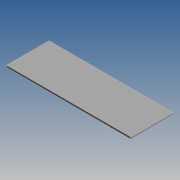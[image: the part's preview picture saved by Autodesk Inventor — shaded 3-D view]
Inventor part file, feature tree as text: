
AUTODESK INVENTOR PART (.ipt)
format: ipt  version: 2015 SP1 (Build 190203100, 203)  size: 176,128 bytes
history: native  units: mm
features: extrude x1, sketch x1
ambient origin geometry x8: Origin, YZ Plane, XZ Plane, XY Plane, X Axis, Y Axis, Z Axis, Center Point
bodies: Solid1 (feature_tree)
feature tree (2):
  extrude  "Extrusion1"  Depth=26.0mm
  sketch  "Sketch1"  dims[d0=76.2mm d1=26.0mm d2=1.2mm d3=0.0mm]
